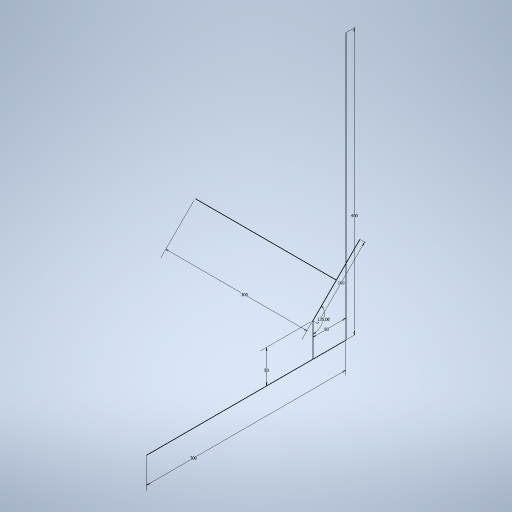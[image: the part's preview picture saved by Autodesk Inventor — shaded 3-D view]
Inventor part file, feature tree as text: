
AUTODESK INVENTOR PART (.ipt)
format: ipt  version: 2024.3 (Build 283343000, 343)  size: 238,592 bytes
history: native  units: mm
features: sketch x1
ambient origin geometry x8: Origin, YZ Plane, XZ Plane, XY Plane, X Axis, Y Axis, Z Axis, Center Point
feature tree (1):
  sketch  "Sketch1"  dims[d0=400.0mm d1=300.0mm d2=50.0mm d3=50.0mm d4=100.0mm d5=135.0deg d6=300.0mm]
